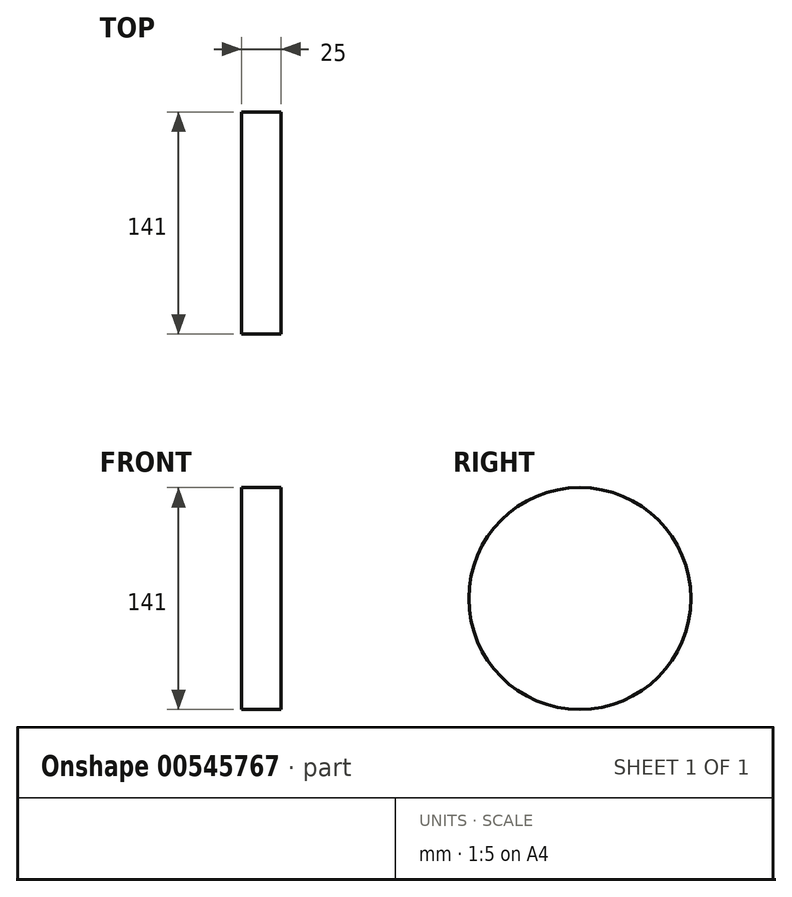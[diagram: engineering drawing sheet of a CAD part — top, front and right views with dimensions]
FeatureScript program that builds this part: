
annotation { "Feature Type Name" : "Feature", "Feature Type Description" : "" }
export const myFeature = defineFeature(function(context is Context, id is Id, definition is map)
    precondition{}
    {
        {
            var Q0;
            Q0=qCreatedBy(makeId("Right.planeOp"),FACE);
            var sketch = newSketch(context, id + "F0", { "sketchPlane" : qUnion([Q0])});
            skCircle(sketch, "E0", {"center": v(0, 0) * mm, "radius": 70.5 * mm});
            skSolve(sketch);
        }
        {
            var Q0;
            Q0=makeQuery(id+"F0.imprint","IMPRINT",FACE,{"disambiguationData":[TD([[makeQuery(id+"F0.imprint","IMPRINT",EDGE,{"derivedFrom":sQuery(id+"F0.wireOp",EDGE,"E0")}),1.0]])]});
            extrude(context, id + "F1", {"entities" : qUnion([Q0]), "depth" : 25 * mm, "offsetDistance" : 25 * mm});
        }
    });
